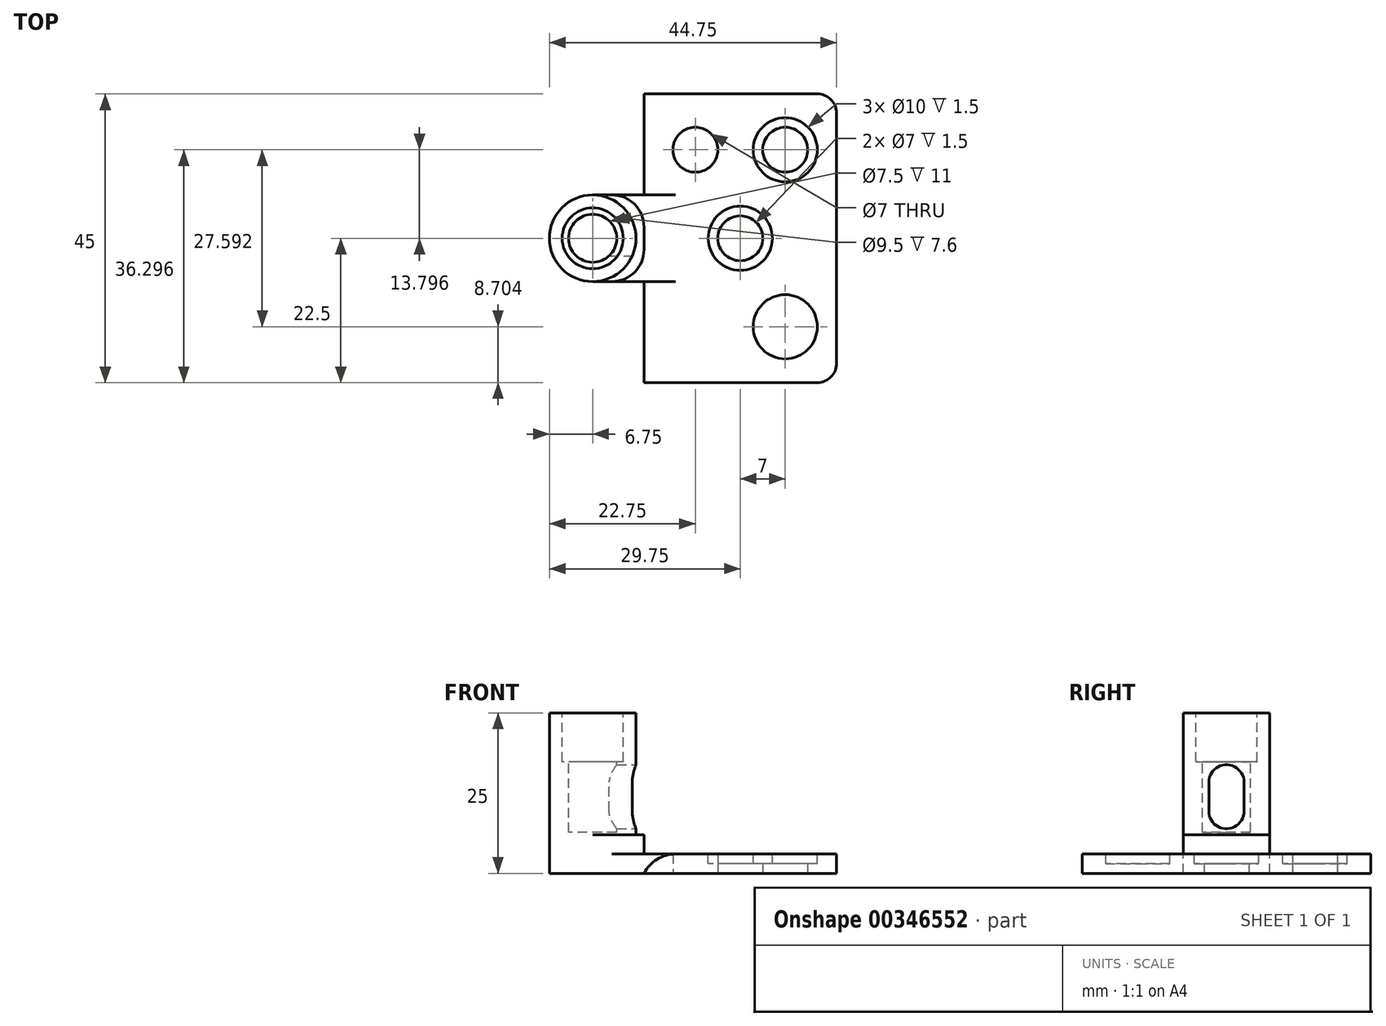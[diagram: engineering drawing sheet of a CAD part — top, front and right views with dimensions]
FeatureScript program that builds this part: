
annotation { "Feature Type Name" : "Feature", "Feature Type Description" : "" }
export const myFeature = defineFeature(function(context is Context, id is Id, definition is map)
    precondition{}
    {
        {
            var Q0;
            Q0=qCreatedBy(makeId("Top.planeOp"),FACE);
            var sketch = newSketch(context, id + "F0", { "sketchPlane" : qUnion([Q0])});
            skLineSegment(sketch, "E0.bottom", {"start": v(-15, 22.5) * mm, "end": v(15, 22.5) * mm});
            skLineSegment(sketch, "E0.top", {"start": v(-15, -22.5) * mm, "end": v(15, -22.5) * mm});
            skLineSegment(sketch, "E0.left", {"start": v(-15, 22.5) * mm, "end": v(-15, -22.5) * mm});
            skLineSegment(sketch, "E0.right", {"start": v(15, 22.5) * mm, "end": v(15, -22.5) * mm});
            skPoint(sketch, "E0.middle", {"position": v(0, 0) * mm});
            skLineSegment(sketch, "E1.bottom", {"start": v(-23, -6.75) * mm, "end": v(-15, -6.75) * mm});
            skLineSegment(sketch, "E1.top", {"start": v(-23, 6.75) * mm, "end": v(-15, 6.75) * mm});
            skCircle(sketch, "E2", {"center": v(-23, 0) * mm, "radius": 6.75 * mm});
            skSolve(sketch);
        }
        {
            var Q0;
            Q0=makeQuery(id+"F0.imprint","IMPRINT",FACE,{"disambiguationData":[TD([[makeQuery(id+"F0.imprint","IMPRINT",EDGE,{"derivedFrom":sQuery(id+"F0.wireOp",EDGE,"E0.bottom")}),-1.0]])]});
            extrude(context, id + "F1", {"entities" : qUnion([Q0]), "depth" : 3 * mm});
        }
        {
            var Q0;
            {var subQ0=sQuery(id+"F0.wireOp",EDGE,"E1.bottom");Q0=makeQuery(id+"F0.imprint","IMPRINT",FACE,{"disambiguationData":[TD([[makeQuery(id+"F0.imprint","IMPRINT",EDGE,{"derivedFrom":subQ0}),1.0]])]});}
            extrude(context, id + "F2", {"entities" : qUnion([Q0]), "operationType" : NewBodyOperationType.ADD, "depth" : 6 * mm});
        }
        {
            var Q0;
            {var subQ0=sQuery(id+"F0.wireOp",EDGE,"E2");var subQ1=makeQuery(id+"F0.imprint","INTERSECT",VERTEX,{"derivedFrom":[sQuery(id+"F0.wireOp",EDGE,"E1.bottom"),subQ0]});Q0=makeQuery(id+"F0.imprint","IMPRINT",FACE,{"disambiguationData":[TD([[makeQuery(id+"F0.imprint","IMPRINT",EDGE,{"disambiguationData":[TD([[subQ1,1.0]])],"derivedFrom":subQ0}),1.0]])]});}
            extrude(context, id + "F3", {"entities" : qUnion([Q0]), "operationType" : NewBodyOperationType.ADD, "depth" : 25 * mm});
        }
        {
            var Q0;
            Q0=makeQuery(id+"F3.opExtrude","CAP_FACE",FACE,{"disambiguationData":[OSD([sQuery(id+"F0.wireOp",EDGE,"E2")])],"isStart":false});
            var sketch = newSketch(context, id + "F4", { "sketchPlane" : qUnion([Q0])});
            skCircle(sketch, "E3", {"center": v(-23, 0) * mm, "radius": 3.75 * mm});
            skSolve(sketch);
        }
        {
            var Q0;
            Q0=makeQuery(id+"F4.imprint","IMPRINT",FACE,{"disambiguationData":[TD([[makeQuery(id+"F4.imprint","IMPRINT",EDGE,{"derivedFrom":sQuery(id+"F4.wireOp",EDGE,"E3")}),1.0]])]});
            extrude(context, id + "F5", {"entities" : qUnion([Q0]), "operationType" : NewBodyOperationType.REMOVE, "oppositeDirection" : true, "depth" : 18.6 * mm});
        }
        {
            var Q0;
            Q0=qCreatedBy(makeId("Right.planeOp"),FACE);
            cPlane(context, id + "F6", {"entities" : qUnion([Q0]), "cplaneType" : CPlaneType.OFFSET, "offset" : 15 * mm, "oppositeDirection" : true, "width" : 150 * mm, "height" : 150 * mm});
        }
        {
            var Q0;
            Q0=qCreatedBy(id+"F6.planeOp",FACE);
            var sketch = newSketch(context, id + "F7", { "sketchPlane" : qUnion([Q0])});
            skArc(sketch, "E4", {"start": v(2.75, 14.19) * mm, "mid": v(0, 16.94) * mm, "end": v(-2.75, 14.19) * mm});
            skArc(sketch, "E5", {"start": v(-2.75, 9.7) * mm, "mid": v(0, 6.95) * mm, "end": v(2.75, 9.7) * mm});
            skLineSegment(sketch, "E6", {"start": v(-2.75, 9.7) * mm, "end": v(-2.75, 14.19) * mm});
            skLineSegment(sketch, "E7", {"start": v(2.75, 9.7) * mm, "end": v(2.75, 14.19) * mm});
            skSolve(sketch);
        }
        {
            var Q0;
            Q0=makeQuery(id+"F7.imprint","IMPRINT",FACE,{"disambiguationData":[TD([[makeQuery(id+"F7.imprint","IMPRINT",EDGE,{"derivedFrom":sQuery(id+"F7.wireOp",EDGE,"E4")}),1.0]])]});
            extrude(context, id + "F8", {"entities" : qUnion([Q0]), "operationType" : NewBodyOperationType.REMOVE, "oppositeDirection" : true, "depth" : 6.13 * mm});
        }
        {
            var Q0;
            {var subQ3=sQuery(id+"F0.wireOp",EDGE,"E0.bottom");Q0=makeQuery(id+"F0.imprint","IMPRINT",FACE,{"disambiguationData":[TD([[makeQuery(id+"F0.imprint","IMPRINT",EDGE,{"derivedFrom":subQ3}),-1.0]])]});}
            var sketch = newSketch(context, id + "F9", { "sketchPlane" : qUnion([Q0])});
            skCircle(sketch, "E8", {"center": v(0, 0) * mm, "radius": 3.5 * mm});
            skCircle(sketch, "E9", {"center": v(7, 13.8) * mm, "radius": 3.5 * mm});
            skCircle(sketch, "E10", {"center": v(-7, 13.8) * mm, "radius": 3.5 * mm});
            skCircle(sketch, "E11.MirrorC", {"center": v(-7, -13.8) * mm, "radius": 3.5 * mm});
            skCircle(sketch, "E12.MirrorC", {"center": v(7, -13.8) * mm, "radius": 3.5 * mm});
            skSolve(sketch);
        }
        {
            var Q0;
            Q0=makeQuery(id+"F9.imprint","IMPRINT",FACE,{"disambiguationData":[TD([[makeQuery(id+"F9.imprint","IMPRINT",EDGE,{"derivedFrom":sQuery(id+"F9.wireOp",EDGE,"E12.MirrorC")}),-1.0]])]});
            var Q1;
            Q1=makeQuery(id+"F9.imprint","IMPRINT",FACE,{"disambiguationData":[TD([[makeQuery(id+"F9.imprint","IMPRINT",EDGE,{"derivedFrom":sQuery(id+"F9.wireOp",EDGE,"E11.MirrorC")}),-1.0]])]});
            var Q2;
            Q2=makeQuery(id+"F9.imprint","IMPRINT",FACE,{"disambiguationData":[TD([[makeQuery(id+"F9.imprint","IMPRINT",EDGE,{"derivedFrom":sQuery(id+"F9.wireOp",EDGE,"E10")}),1.0]])]});
            var Q3;
            Q3=makeQuery(id+"F9.imprint","IMPRINT",FACE,{"disambiguationData":[TD([[makeQuery(id+"F9.imprint","IMPRINT",EDGE,{"derivedFrom":sQuery(id+"F9.wireOp",EDGE,"E9")}),1.0]])]});
            var Q4;
            Q4=makeQuery(id+"F9.imprint","IMPRINT",FACE,{"disambiguationData":[TD([[makeQuery(id+"F9.imprint","IMPRINT",EDGE,{"derivedFrom":sQuery(id+"F9.wireOp",EDGE,"E8")}),1.0]])]});
            extrude(context, id + "F10", {"entities" : qUnion([Q0, Q1, Q2, Q3, Q4]), "operationType" : NewBodyOperationType.REMOVE, "depth" : 3 * mm});
        }
        {
            var Q0;
            Q0=makeQuery(id+"F1.opExtrude","CAP_FACE",FACE,{"disambiguationData":[OSD([sQuery(id+"F0.wireOp",EDGE,"E0.bottom"),sQuery(id+"F0.wireOp",EDGE,"E0.top"),sQuery(id+"F0.wireOp",EDGE,"E0.left"),sQuery(id+"F0.wireOp",EDGE,"E0.right")])],"isStart":false});
            var sketch = newSketch(context, id + "F11", { "sketchPlane" : qUnion([Q0])});
            skCircle(sketch, "E13", {"center": v(7, 13.8) * mm, "radius": 5 * mm});
            skCircle(sketch, "E14", {"center": v(-7, 13.8) * mm, "radius": 5 * mm});
            skCircle(sketch, "E15", {"center": v(0, 0) * mm, "radius": 5 * mm});
            skCircle(sketch, "E16", {"center": v(7, -13.8) * mm, "radius": 5 * mm});
            skCircle(sketch, "E17", {"center": v(-7, -13.8) * mm, "radius": 5 * mm});
            skSolve(sketch);
        }
        {
            var Q0;
            Q0=makeQuery(id+"F11.imprint","IMPRINT",FACE,{"disambiguationData":[TD([[makeQuery(id+"F11.imprint","IMPRINT",EDGE,{"derivedFrom":makeQuery(id+"F10.boolean.opBoolean","COPY",EDGE,{"derivedFrom":makeQuery(id+"F10.opExtrude","CAP_EDGE",EDGE,{"disambiguationData":[OSD([sQuery(id+"F9.wireOp",EDGE,"E10")])],"isStart":false})})}),-1.0]])]});
            var Q1;
            Q1=makeQuery(id+"F11.imprint","IMPRINT",FACE,{"disambiguationData":[TD([[makeQuery(id+"F11.imprint","IMPRINT",EDGE,{"derivedFrom":sQuery(id+"F11.wireOp",EDGE,"E13")}),1.0]])]});
            var Q2;
            Q2=makeQuery(id+"F11.imprint","IMPRINT",FACE,{"disambiguationData":[TD([[makeQuery(id+"F11.imprint","IMPRINT",EDGE,{"derivedFrom":sQuery(id+"F11.wireOp",EDGE,"E15")}),1.0]])]});
            var Q3;
            Q3=makeQuery(id+"F11.imprint","IMPRINT",FACE,{"disambiguationData":[TD([[makeQuery(id+"F11.imprint","IMPRINT",EDGE,{"derivedFrom":sQuery(id+"F11.wireOp",EDGE,"E16")}),1.0]])]});
            var Q4;
            Q4=makeQuery(id+"F11.imprint","IMPRINT",FACE,{"disambiguationData":[TD([[makeQuery(id+"F11.imprint","IMPRINT",EDGE,{"derivedFrom":makeQuery(id+"F10.boolean.opBoolean","COPY",EDGE,{"derivedFrom":makeQuery(id+"F10.opExtrude","CAP_EDGE",EDGE,{"disambiguationData":[OSD([sQuery(id+"F9.wireOp",EDGE,"E11.MirrorC")])],"isStart":false})})}),1.0]])]});
            extrude(context, id + "F12", {"entities" : qUnion([Q0, Q1, Q2, Q3, Q4]), "operationType" : NewBodyOperationType.REMOVE, "oppositeDirection" : true, "depth" : 1.5 * mm});
        }
        {
            var Q0;
            {var subQ0=sQuery(id+"F0.wireOp",EDGE,"E0.left");Q0=makeQuery(id+"F2.boolean.opBoolean","SPLIT",EDGE,{"disambiguationData":[topologyDisambiguationEdgeConnected([makeQuery(id+"F1.opExtrude","CAP_FACE",FACE,{"disambiguationData":[OSD([sQuery(id+"F0.wireOp",EDGE,"E0.bottom"),sQuery(id+"F0.wireOp",EDGE,"E0.top"),subQ0,sQuery(id+"F0.wireOp",EDGE,"E0.right")])],"isStart":false}),makeQuery(id+"F2.opExtrude","SWEPT_FACE",FACE,{"disambiguationData":[OSD([subQ0])]})])],"derivedFrom":makeQuery(id+"F1.opExtrude","CAP_EDGE",EDGE,{"disambiguationData":[OSD([subQ0])],"isStart":false})});}
            fillet(context, id + "F13", {"entities" : qUnion([Q0]), "radius" : 5.5 * mm, "tangentPropagation" : true, "allowEdgeOverflow" : false});
        }
        {
            var Q0;
            {var subQ0=sQuery(id+"F0.wireOp",EDGE,"E0.left");Q0=makeQuery(id+"F13.opFillet","TWEAK_EDGE",EDGE,{"derivedFrom":[makeQuery(id+"F2.boolean.opBoolean","TWEAK_VERTEX",VERTEX,{"derivedFrom":[makeQuery(id+"F1.opExtrude","CAP_FACE",FACE,{"disambiguationData":[OSD([sQuery(id+"F0.wireOp",EDGE,"E0.bottom"),sQuery(id+"F0.wireOp",EDGE,"E0.top"),subQ0,sQuery(id+"F0.wireOp",EDGE,"E0.right")])],"isStart":false}),makeQuery(id+"F1.opExtrude","SWEPT_FACE",FACE,{"disambiguationData":[OSD([subQ0])]}),makeQuery(id+"F2.opExtrude","SWEPT_FACE",FACE,{"disambiguationData":[OSD([subQ0])]}),makeQuery(id+"F2.opExtrude","SWEPT_FACE",FACE,{"disambiguationData":[OSD([sQuery(id+"F0.wireOp",EDGE,"E1.bottom")])]})]})]});}
            var Q1;
            {var subQ0=sQuery(id+"F0.wireOp",EDGE,"E0.left");Q1=makeQuery(id+"F13.opFillet","TWEAK_EDGE",EDGE,{"derivedFrom":[makeQuery(id+"F2.boolean.opBoolean","TWEAK_VERTEX",VERTEX,{"derivedFrom":[makeQuery(id+"F1.opExtrude","CAP_FACE",FACE,{"disambiguationData":[OSD([sQuery(id+"F0.wireOp",EDGE,"E0.bottom"),sQuery(id+"F0.wireOp",EDGE,"E0.top"),subQ0,sQuery(id+"F0.wireOp",EDGE,"E0.right")])],"isStart":false}),makeQuery(id+"F1.opExtrude","SWEPT_FACE",FACE,{"disambiguationData":[OSD([subQ0])]}),makeQuery(id+"F2.opExtrude","SWEPT_FACE",FACE,{"disambiguationData":[OSD([subQ0])]}),makeQuery(id+"F2.opExtrude","SWEPT_FACE",FACE,{"disambiguationData":[OSD([sQuery(id+"F0.wireOp",EDGE,"E1.top")])]})]})]});}
            var Q2;
            {var subQ0=sQuery(id+"F0.wireOp",EDGE,"E0.left");var subQ1=sQuery(id+"F0.wireOp",EDGE,"E1.top");Q2=makeQuery(id+"F2.boolean.opBoolean","SPLIT",EDGE,{"disambiguationData":[topologyDisambiguationEdgeConnected([makeQuery(id+"F1.opExtrude","SWEPT_FACE",FACE,{"disambiguationData":[OSD([subQ0])]})])],"derivedFrom":makeQuery(id+"F2.opExtrude","SWEPT_EDGE",EDGE,{"disambiguationData":[OSD([subQ0,subQ1])]})});}
            var Q3;
            {var subQ0=sQuery(id+"F0.wireOp",EDGE,"E0.left");var subQ1=sQuery(id+"F0.wireOp",EDGE,"E1.bottom");Q3=makeQuery(id+"F2.boolean.opBoolean","SPLIT",EDGE,{"disambiguationData":[topologyDisambiguationEdgeConnected([makeQuery(id+"F1.opExtrude","SWEPT_FACE",FACE,{"disambiguationData":[OSD([subQ0])]})])],"derivedFrom":makeQuery(id+"F2.opExtrude","SWEPT_EDGE",EDGE,{"disambiguationData":[OSD([subQ0,subQ1])]})});}
            fillet(context, id + "F14", {"entities" : qUnion([Q0, Q1, Q2, Q3]), "radius" : 5 * mm, "tangentPropagation" : true, "allowEdgeOverflow" : false});
        }
        {
            var Q0;
            Q0=makeQuery(id+"F1.opExtrude","SWEPT_EDGE",EDGE,{"disambiguationData":[OSD([sQuery(id+"F0.wireOp",EDGE,"E0.bottom"),sQuery(id+"F0.wireOp",EDGE,"E0.right")])]});
            var Q1;
            Q1=makeQuery(id+"F1.opExtrude","SWEPT_EDGE",EDGE,{"disambiguationData":[OSD([sQuery(id+"F0.wireOp",EDGE,"E0.top"),sQuery(id+"F0.wireOp",EDGE,"E0.right")])]});
            var Q2;
            Q2=makeQuery(id+"F1.opExtrude","SWEPT_EDGE",EDGE,{"disambiguationData":[OSD([sQuery(id+"F0.wireOp",EDGE,"E0.top"),sQuery(id+"F0.wireOp",EDGE,"E0.left")])]});
            var Q3;
            Q3=makeQuery(id+"F1.opExtrude","SWEPT_EDGE",EDGE,{"disambiguationData":[OSD([sQuery(id+"F0.wireOp",EDGE,"E0.bottom"),sQuery(id+"F0.wireOp",EDGE,"E0.left")])]});
            fillet(context, id + "F15", {"entities" : qUnion([Q0, Q1, Q2, Q3]), "radius" : 3 * mm, "tangentPropagation" : true, "allowEdgeOverflow" : false});
        }
        {
            var Q0;
            Q0=makeQuery(id+"F3.opExtrude","CAP_FACE",FACE,{"disambiguationData":[OSD([sQuery(id+"F0.wireOp",EDGE,"E2")])],"isStart":false});
            var sketch = newSketch(context, id + "F16", { "sketchPlane" : qUnion([Q0])});
            skCircle(sketch, "E18", {"center": v(-23, 0) * mm, "radius": 4.75 * mm});
            skSolve(sketch);
        }
        {
            var Q0;
            Q0=makeQuery(id+"F16.imprint","IMPRINT",FACE,{"disambiguationData":[TD([[makeQuery(id+"F16.imprint","IMPRINT",EDGE,{"derivedFrom":sQuery(id+"F16.wireOp",EDGE,"E18")}),1.0]])]});
            extrude(context, id + "F17", {"entities" : qUnion([Q0]), "operationType" : NewBodyOperationType.REMOVE, "oppositeDirection" : true, "depth" : 7.6 * mm});
        }
    });
